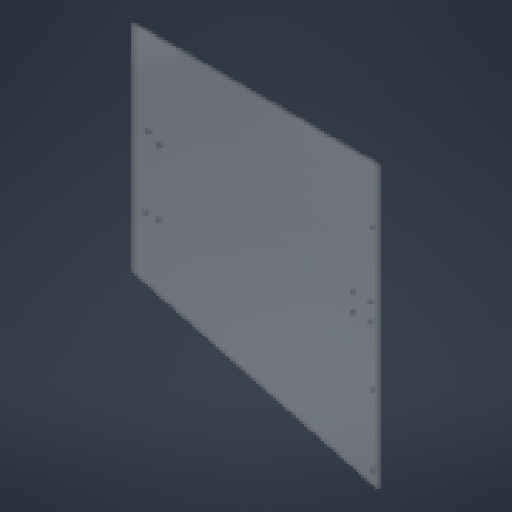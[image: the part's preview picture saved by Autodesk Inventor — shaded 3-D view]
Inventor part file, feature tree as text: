
AUTODESK INVENTOR PART (.ipt)
format: ipt  version: 2024.3 (Build 283343010, 343A)  size: 172,032 bytes
history: native  units: in
note: dims shown in document units (in); Inventor stores cm internally (conversion verified against a paired STEP export)
features: sketch x6, other x5, hole x4, projected_geometry x2, reference x2, sheet_metal_op x1
ambient origin geometry x8: Origin, YZ Plane, XZ Plane, XY Plane, X Axis, Y Axis, Z Axis, Center Point
bodies: Solid1 (feature_tree)
feature tree (20):
  sheet_metal_op  "Face1"
  hole  "Hole1"  [1 undecoded]
  hole  "Hole2"  [1 undecoded]
  hole  "Hole3"  [1 undecoded]
  hole  "Hole4"  [1 undecoded]
  sketch  "Sketch1"  dims[d0=14.0in d1=16.0in]
  other  "Plate1"
  sketch  "Sketch2"  dims[d2=0.12in d3=15.0deg]
  projected_geometry  "Projected Loop1"
  sketch  "Sketch3"  dims[d4=0.12in d5=0.0in]
  projected_geometry  "Projected Loop2"
  sketch  "Sketch4"  dims[d6=0.5in d7=0.7874in d9=1.0in d10=0.7874in d12=1.0in]
  sketch  "Sketch5"  dims[d15=0.201in d16=0.75in d17=0.385in d18=0.25in d19=0.5635in d20=0.12in]
  reference  "Reference1"
  reference  "Reference2"
  sketch  "Sketch6"  dims[d21=0.8108in d22=0.3505in d23=4.0in d24=0.75in d25=8.0in d26=0.201in d27=0.75in d28=0.375in d29=0.25in d30=0.5635in d31=0.12in d32=0.8108in d33=0.201in d34=0.75in d35=0.375in d36=0.25in d37=0.5635in d38=0.12in d39=0.8108in d40=0.75in d41=0.875in d42=0.25in d43=0.75in d44=0.375in d45=0.25in d46=0.5635in d47=0.12in d48=0.8108in]
  other  "Cut1"
  other  "<userpath>\Documents\GitHub\2025-Poseidon-Mechanical\#Poseidon 2025.iam"
  other  "#Poseidon 2025.iam"
  other  "Part Studio 1 - Support 2:1"
note: 4 required parameter values undecoded (feature->parameter linkage not recoverable at this tier; creation-order binding heuristic only, values carry confidence <= 0.55)
